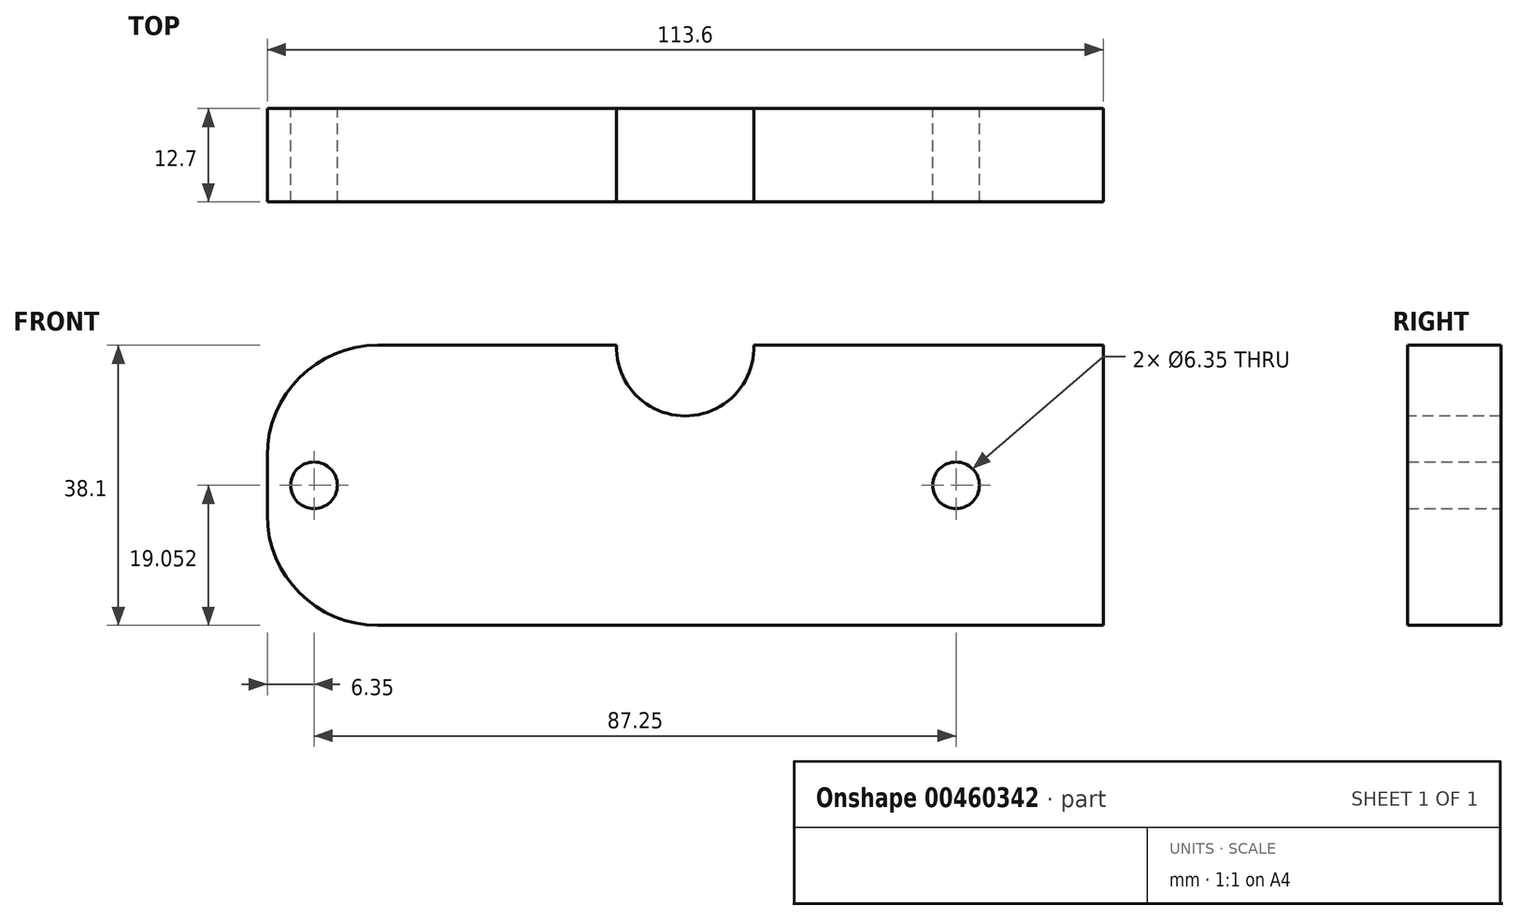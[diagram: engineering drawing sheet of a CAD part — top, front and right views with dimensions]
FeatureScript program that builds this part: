
annotation { "Feature Type Name" : "Feature", "Feature Type Description" : "" }
export const myFeature = defineFeature(function(context is Context, id is Id, definition is map)
    precondition{}
    {
        {
            var Q0;
            Q0=qCreatedBy(makeId("Front.planeOp"),FACE);
            var sketch = newSketch(context, id + "F0", { "sketchPlane" : qUnion([Q0])});
            skLineSegment(sketch, "E0.bottom", {"start": v(56.8, 13.34) * mm, "end": v(-56.8, 13.34) * mm});
            skLineSegment(sketch, "E0.top", {"start": v(56.8, 51.44) * mm, "end": v(-56.8, 51.44) * mm});
            skLineSegment(sketch, "E0.left", {"start": v(56.8, 13.34) * mm, "end": v(56.8, 51.44) * mm});
            skLineSegment(sketch, "E0.right", {"start": v(-56.8, 13.34) * mm, "end": v(-56.8, 51.44) * mm});
            skPoint(sketch, "E0.middle", {"position": v(0, 32.4) * mm});
            skLineSegment(sketch, "E1", {"start": v(-56.8, 32.4) * mm, "end": v(45.41, 32.4) * mm, "construction": true});
            skPoint(sketch, "E1.endSnap0", {"position": v(-56.8, 32.4) * mm});
            skCircle(sketch, "E2", {"center": v(-50.45, 32.4) * mm, "radius": 3.17 * mm});
            skCircle(sketch, "E3", {"center": v(36.8, 32.4) * mm, "radius": 3.17 * mm});
            skSolve(sketch);
        }
        {
            var Q0;
            Q0=qSketchRegion(id+"F0",true);
            extrude(context, id + "F1", {"entities" : qUnion([Q0]), "depth" : 12.7 * mm});
        }
        {
            var Q0;
            Q0=makeQuery(id+"F1.opExtrude","SWEPT_EDGE",EDGE,{"disambiguationData":[OSD([sQuery(id+"F0.wireOp",EDGE,"E0.top"),sQuery(id+"F0.wireOp",EDGE,"E0.right")])]});
            var Q1;
            Q1=makeQuery(id+"F1.opExtrude","SWEPT_EDGE",EDGE,{"disambiguationData":[OSD([sQuery(id+"F0.wireOp",EDGE,"E0.bottom"),sQuery(id+"F0.wireOp",EDGE,"E0.right")])]});
            fillet(context, id + "F2", {"entities" : qUnion([Q0, Q1]), "radius" : 15 * mm, "tangentPropagation" : true, "allowEdgeOverflow" : false});
        }
        {
            var Q0;
            Q0=makeQuery(id+"F1.opExtrude","CAP_FACE",FACE,{"disambiguationData":[OSD([sQuery(id+"F0.wireOp",EDGE,"E0.bottom"),sQuery(id+"F0.wireOp",EDGE,"E0.top"),sQuery(id+"F0.wireOp",EDGE,"E0.left"),sQuery(id+"F0.wireOp",EDGE,"E0.right"),sQuery(id+"F0.wireOp",EDGE,"E2"),sQuery(id+"F0.wireOp",EDGE,"Ag98GLvs-puQg-92uF-8dMV-TIUTNT0F0FqC"),sQuery(id+"F0.wireOp",EDGE,"wgJ8hgVP-P0Pc-yske-DRwo-g0lwUWk7A8nh")])],"isStart":false});
            var sketch = newSketch(context, id + "F3", { "sketchPlane" : qUnion([Q0])});
            skCircle(sketch, "E4", {"center": v(0, 51.18) * mm, "radius": 9.34 * mm});
            skLineSegment(sketch, "E5", {"start": v(-56.8, 32.4) * mm, "end": v(-56.8, 55.24) * mm, "construction": true});
            skSolve(sketch);
        }
        {
            var Q0;
            Q0=qSketchRegion(id+"F3",true);
            extrude(context, id + "F4", {"entities" : qUnion([Q0]), "operationType" : NewBodyOperationType.REMOVE, "oppositeDirection" : true, "depth" : 15.4 * mm});
        }
    });
